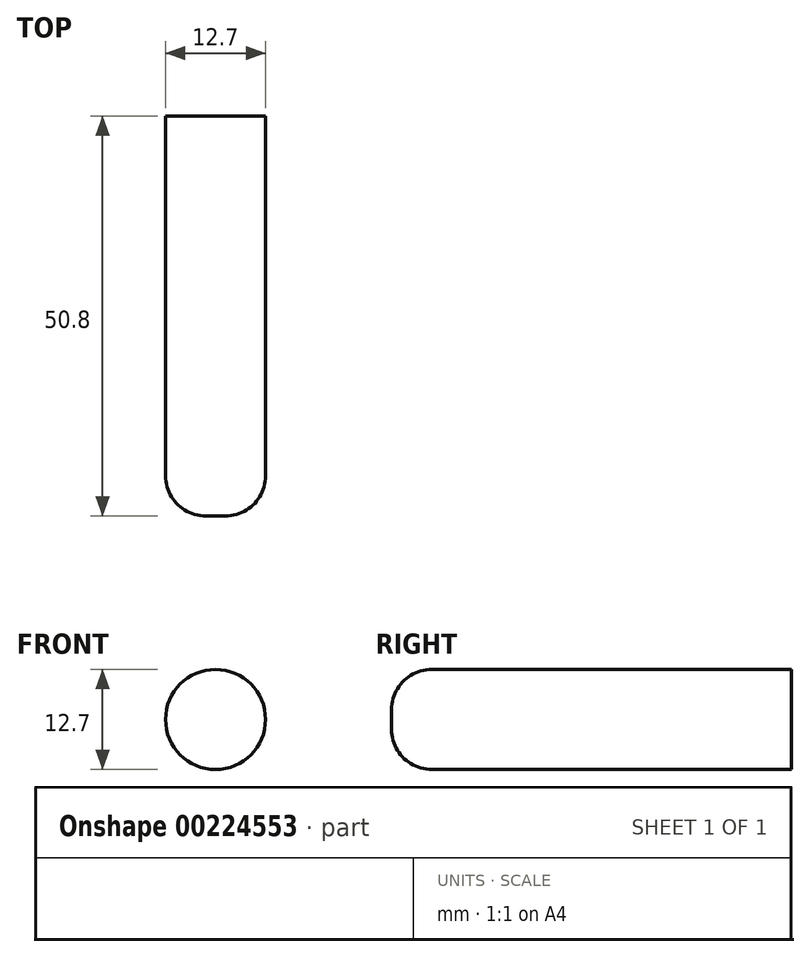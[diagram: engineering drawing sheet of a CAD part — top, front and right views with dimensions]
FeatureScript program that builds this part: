
annotation { "Feature Type Name" : "Feature", "Feature Type Description" : "" }
export const myFeature = defineFeature(function(context is Context, id is Id, definition is map)
    precondition{}
    {
        {
            var Q0;
            Q0=qCreatedBy(makeId("Front.planeOp"),FACE);
            var sketch = newSketch(context, id + "F0", { "sketchPlane" : qUnion([Q0])});
            skCircle(sketch, "E0", {"center": v(0, 0) * mm, "radius": 6.35 * mm});
            skSolve(sketch);
        }
        {
            var Q0;
            Q0=makeQuery(id+"F0.imprint","IMPRINT",FACE,{"disambiguationData":[TD([[makeQuery(id+"F0.imprint","IMPRINT",EDGE,{"derivedFrom":sQuery(id+"F0.wireOp",EDGE,"E0")}),1.0]])]});
            extrude(context, id + "F1", {"entities" : qUnion([Q0]), "depth" : 50.8 * mm});
        }
        {
            var Q0;
            Q0=makeQuery(id+"F1.opExtrude","CAP_FACE",FACE,{"disambiguationData":[OSD([sQuery(id+"F0.wireOp",EDGE,"E0")])],"isStart":false});
            fillet(context, id + "F2", {"entities" : qUnion([Q0]), "radius" : 5.08 * mm, "tangentPropagation" : true, "allowEdgeOverflow" : false});
        }
    });
